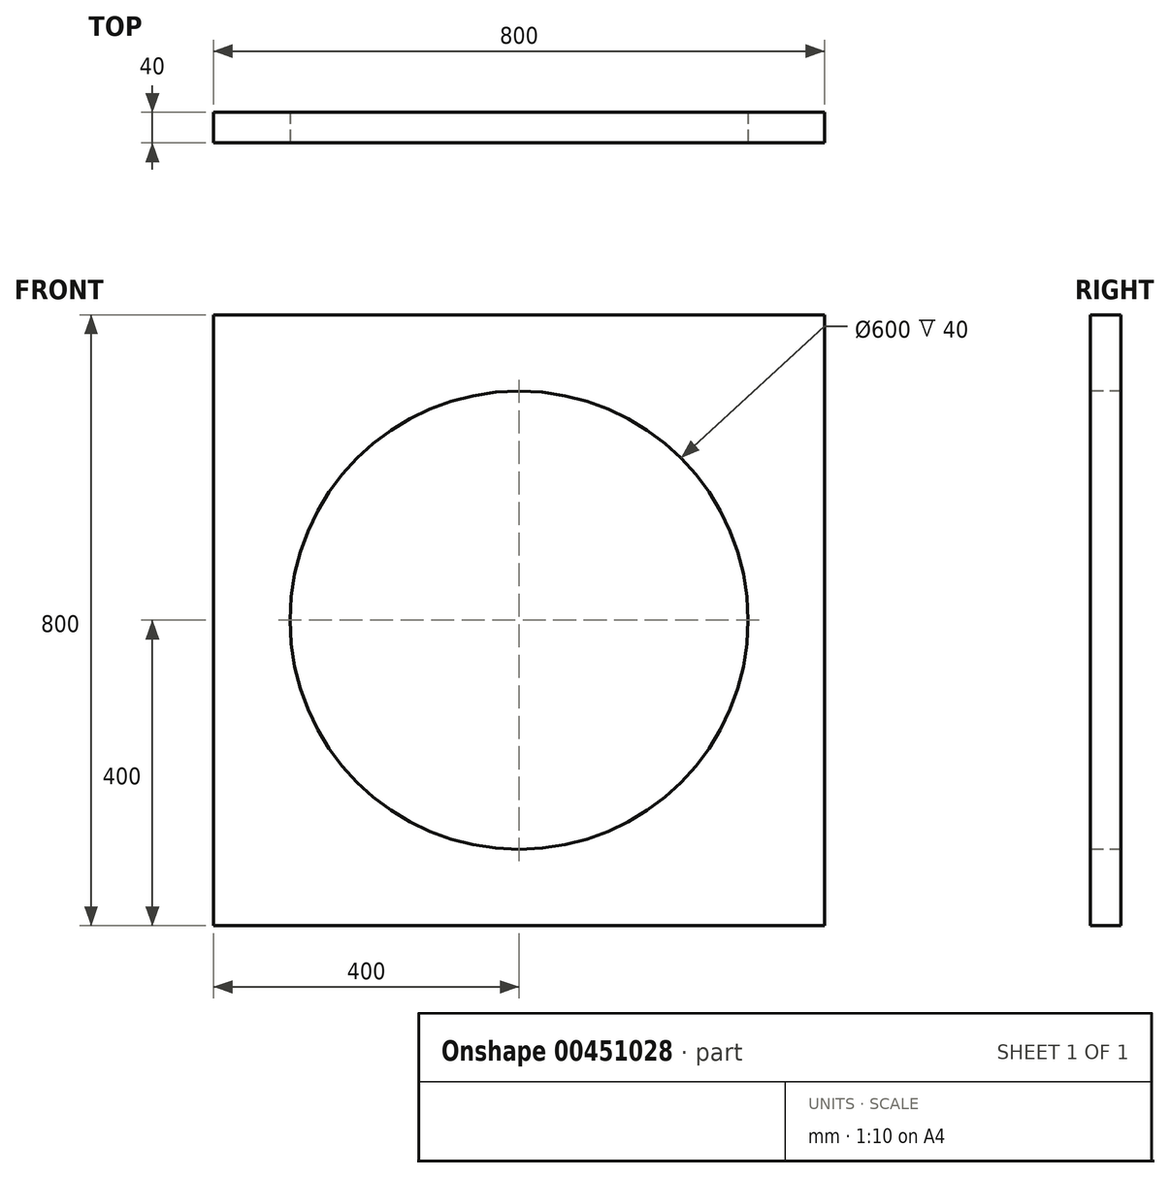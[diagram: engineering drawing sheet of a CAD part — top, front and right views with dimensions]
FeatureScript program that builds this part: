
annotation { "Feature Type Name" : "Feature", "Feature Type Description" : "" }
export const myFeature = defineFeature(function(context is Context, id is Id, definition is map)
    precondition{}
    {
        {
            var Q0;
            Q0=qCreatedBy(makeId("Front.planeOp"),FACE);
            var sketch = newSketch(context, id + "F0", { "sketchPlane" : qUnion([Q0])});
            skLineSegment(sketch, "E0.bottom", {"start": v(400, 400) * mm, "end": v(-400, 400) * mm});
            skLineSegment(sketch, "E0.top", {"start": v(400, -400) * mm, "end": v(-400, -400) * mm});
            skLineSegment(sketch, "E0.left", {"start": v(400, 400) * mm, "end": v(400, -400) * mm});
            skLineSegment(sketch, "E0.right", {"start": v(-400, 400) * mm, "end": v(-400, -400) * mm});
            skPoint(sketch, "E0.middle", {"position": v(0, 0) * mm});
            skSolve(sketch);
        }
        {
            var Q0;
            Q0 = qSketchRegion(id + "F0", true);
            extrude(context, id + "F1", {"entities" : qUnion([Q0]), "oppositeDirection" : true, "depth" : 40 * mm});
        }
        {
            var Q0;
            Q0=makeQuery(id+"F1.opExtrude","CAP_FACE",FACE,{"disambiguationData":[OSD([sQuery(id+"F0.wireOp",EDGE,"E0.bottom"),sQuery(id+"F0.wireOp",EDGE,"E0.top"),sQuery(id+"F0.wireOp",EDGE,"E0.left"),sQuery(id+"F0.wireOp",EDGE,"E0.right")])],"isStart":true});
            var sketch = newSketch(context, id + "F2", { "sketchPlane" : qUnion([Q0])});
            skCircle(sketch, "E1", {"center": v(0, 0) * mm, "radius": 300 * mm});
            skSolve(sketch);
        }
        {
            var Q0;
            Q0=sQuery(id+"F2.wireOp",VERTEX,"E1.center");
            var Q1;
            Q1=makeQuery(id+"F1.opExtrude","SWEPT_BODY",BODY,{"disambiguationData":[OSD([sQuery(id+"F0.wireOp",EDGE,"E0.bottom"),sQuery(id+"F0.wireOp",EDGE,"E0.top"),sQuery(id+"F0.wireOp",EDGE,"E0.left"),sQuery(id+"F0.wireOp",EDGE,"E0.right")])]});
            hole(context, id + "F3", {"style" : HoleStyle.SIMPLE, "endStyle" : HoleEndStyle.THROUGH, "holeDiameter" : 600 * mm, "isTappedThrough" : true, "tappedDepth" : 12 * mm, "tapClearance" : 3, "locations" : qUnion([Q0]), "scope" : qUnion([Q1])});
        }
    });
